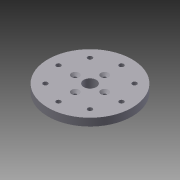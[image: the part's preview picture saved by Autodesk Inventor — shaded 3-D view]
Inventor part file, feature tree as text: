
AUTODESK INVENTOR PART (.ipt)
format: ipt  version: 2012 SP1 (Build 160190100, 190)  size: 155,648 bytes
history: native  units: in
note: dims shown in document units (in); Inventor stores cm internally (conversion verified against a paired STEP export)
features: sketch x3, hole x2, pattern_circular x2, revolve x1
ambient origin geometry x8: Origin, YZ Plane, XZ Plane, XY Plane, X Axis, Y Axis, Z Axis, Center Point
bodies: Solid1 (feature_tree)
feature tree (8):
  revolve  "Revolution1"  [1 undecoded]
  hole  "Hole2"  [1 undecoded]
  pattern_circular  "Circular Pattern2"  [2 undecoded]
  hole  "Hole3"  [1 undecoded]
  pattern_circular  "Circular Pattern3"  [2 undecoded]
  sketch  "Sketch1"  dims[d0=0.1732in d1=0.5295in]
  sketch  "Sketch3"  dims[d2=1.7717in d3=3.937in]
  sketch  "Sketch5"  dims[d4=90.0deg d16=1.4764in d17=0.2165in d18=0.2362in d19=0.4488in d20=0.0787in d21=90.0deg d22=0.315in d23=0.8108in d24=3.1496in d25=360.0deg d28=0.591in d29=0.689in d30=0.1495in d31=0.2362in d32=0.3543in d33=0.0787in d34=0.5635in d35=0.315in d36=0.8108in d37=1.5748in d38=360.0deg d40=1.0965in d41=0.9528in d42=0.0472in]
note: 7 required parameter values undecoded (feature->parameter linkage not recoverable at this tier; creation-order binding heuristic only, values carry confidence <= 0.55)